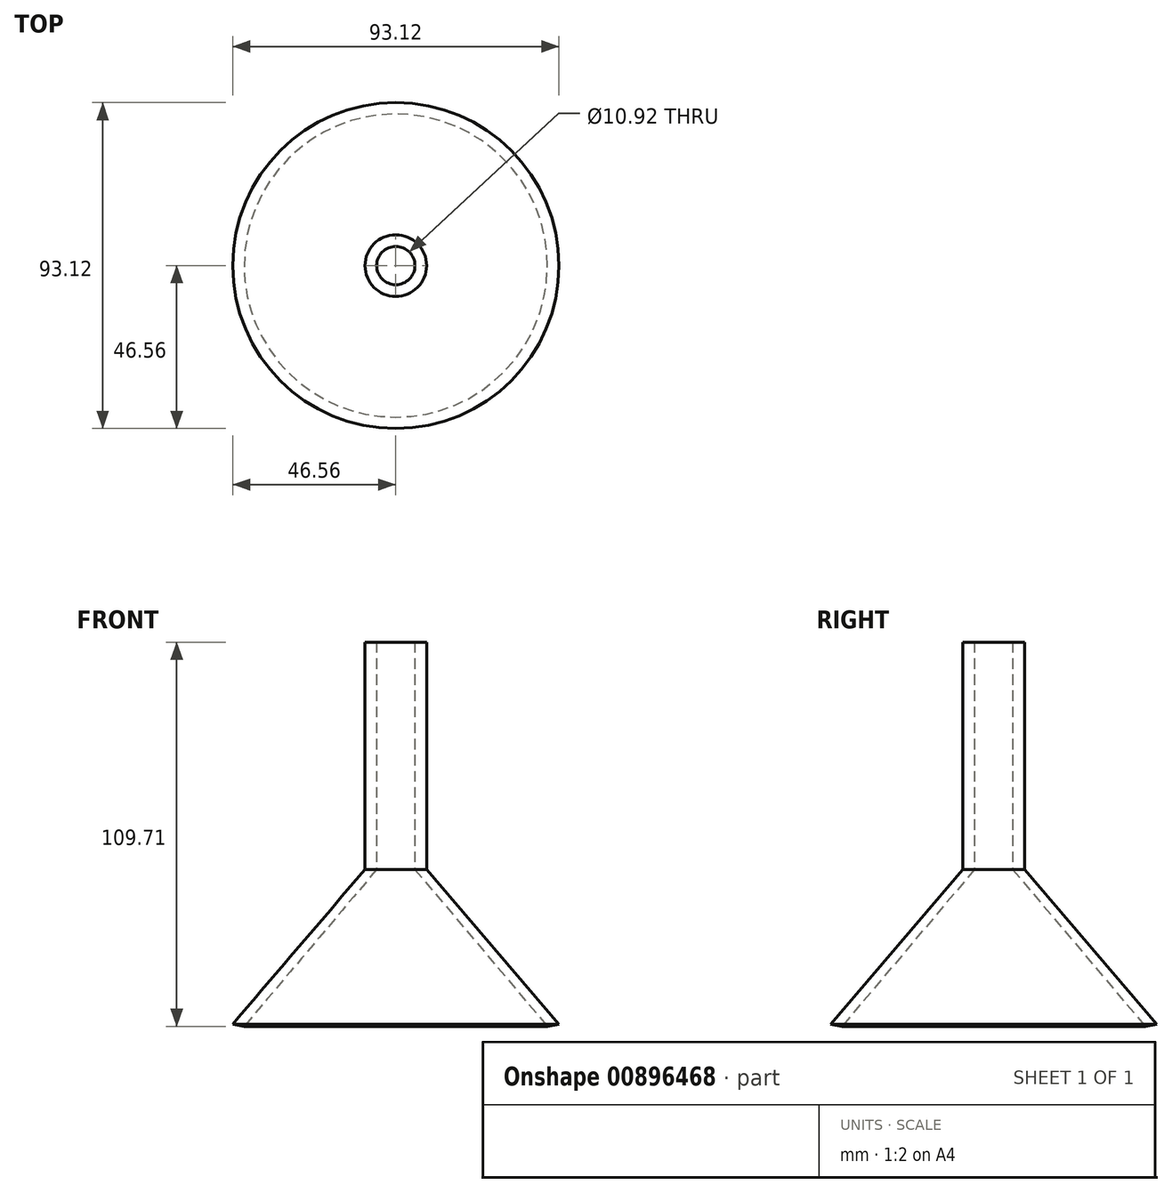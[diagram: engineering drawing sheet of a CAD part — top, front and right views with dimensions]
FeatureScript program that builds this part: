
annotation { "Feature Type Name" : "Feature", "Feature Type Description" : "" }
export const myFeature = defineFeature(function(context is Context, id is Id, definition is map)
    precondition{}
    {
        {
            var Q0;
            Q0=qCreatedBy(makeId("Front.planeOp"),FACE);
            var sketch = newSketch(context, id + "F0", { "sketchPlane" : qUnion([Q0])});
            skLineSegment(sketch, "E0", {"start": v(0, 0) * mm, "end": v(0, 62.15) * mm});
            skLineSegment(sketch, "E1", {"start": v(0, 0) * mm, "end": v(0, 62.15) * mm, "construction": true});
            skLineSegment(sketch, "E2", {"start": v(8.8, 64.9) * mm, "end": v(8.8, 0) * mm});
            skLineSegment(sketch, "E3", {"start": v(8.8, 0) * mm, "end": v(46.56, -44.16) * mm});
            skLineSegment(sketch, "E4", {"start": v(8.8, 64.9) * mm, "end": v(5.46, 64.9) * mm});
            skLineSegment(sketch, "E5", {"start": v(5.46, 64.9) * mm, "end": v(5.46, 0) * mm});
            skLineSegment(sketch, "E6", {"start": v(5.46, 0) * mm, "end": v(43.29, -44.8) * mm});
            skLineSegment(sketch, "E7", {"start": v(43.29, -44.8) * mm, "end": v(46.56, -44.16) * mm});
            skSolve(sketch);
        }
        {
            var Q0;
            Q0 = qSketchRegion(id + "F0", true);
            var Q1;
            Q1=sQuery(id+"F0.wireOp",EDGE,"E0");
            revolve(context, id + "F1", {"surfaceOperationType" : NewSurfaceOperationType.NEW, "entities" : qUnion([Q0]), "axis" : qUnion([Q1]), "revolveType" : RevolveType.FULL});
        }
    });
